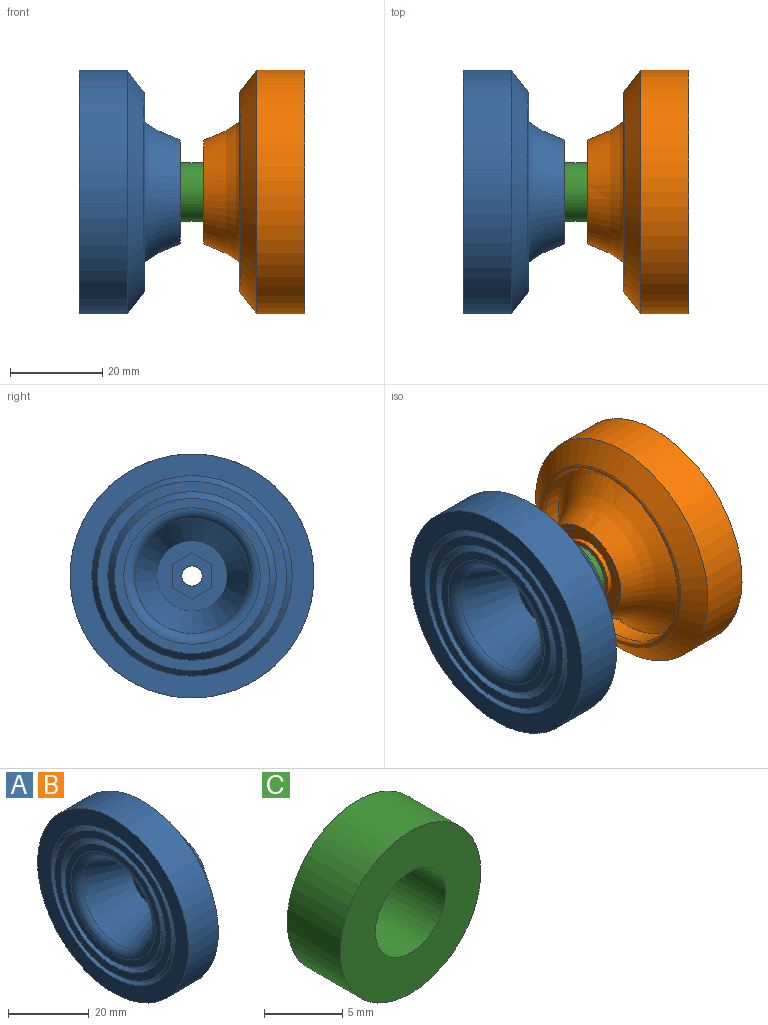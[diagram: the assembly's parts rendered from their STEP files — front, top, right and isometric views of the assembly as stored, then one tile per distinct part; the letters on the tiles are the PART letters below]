
ASSEMBLY  parts=3 mates=2
PART A: 34 faces, bbox 28.5x72.3x72.3 mm
  f0: cylinder r=2.2mm len=5.87mm, axis (1,0,0), area 81.1mm2, adj f17,f33
  f1: plane 22.55x22.55mm, normal (1,0,0), area 66.1mm2, adj f2,f26
  f2: torus R=33.4mm, axis (1,0,0), area 1516.3mm2, adj f1,f3
  f3: cylinder r=20.5mm len=41mm, axis (1,0,0), area 519.1mm2, adj f2,f4
  f4: torus R=21.3mm, axis (1,0,0), area 237.4mm2, adj f3,f5
  f5: torus R=104.59mm, axis (1,0,0), area 897.4mm2, adj f4,f6
  f6: cylinder r=26.5mm len=53mm, axis (1,0,0), area 1743.5mm2, adj f5,f7
  f7: plane 53x53mm, normal (-1,0,0), area 715.6mm2, adj f6,f8
  f8: cylinder r=21.78mm len=43.56mm, axis (1,0,0), area 273.7mm2, adj f7,f9
  f9: cone r=21.78mm half-angle=31.4deg, axis (1,0,0), area 311.7mm2, adj f8,f10
  f10: plane 41.12x41.12mm, normal (-1,0,0), area 276.3mm2, adj f9,f11
  f11: cylinder r=18.3mm len=36.6mm, axis (1,0,0), area 229.9mm2, adj f10,f12
  f12: cone r=18.3mm half-angle=35.9deg, axis (1,0,0), area 272.7mm2, adj f11,f13
  f13: plane 33.7x33.7mm, normal (-1,0,0), area 202.4mm2, adj f12,f14
  f14: torus R=14.81mm, axis (1,0,0), area 254.7mm2, adj f13,f15
  f15: cone r=12.48mm half-angle=21.1deg, axis (-1,0,0), area 849.5mm2, adj f14,f16
  f16: plane 15.28x15.28mm, normal (-1,0,0), area 118.5mm2, adj f15,f27,f28,f29,f30,f31,f32
  f17: plane 6x6mm, normal (1,0,0), area 13.1mm2, adj f0,f18
  f18: cylinder r=3mm len=6mm, axis (1,0,0), area 33mm2, adj f17,f19
  f19: plane 7.6x7.6mm, normal (1,0,0), area 17.1mm2, adj f18,f20
  f20: cylinder r=3.8mm len=7.6mm, axis (1,0,0), area 17.9mm2, adj f19,f21
  f21: plane 13x13mm, normal (1,0,0), area 87.4mm2, adj f20,f22
  f22: cylinder r=6.5mm len=13mm, axis (1,0,0), area 61.3mm2, adj f21,f23
  f23: plane 14.6x14.6mm, normal (1,0,0), area 34.7mm2, adj f22,f24
  f24: cylinder r=7.3mm len=14.6mm, axis (1,0,0), area 49.3mm2, adj f23,f25
  f25: plane 20.6x20.6mm, normal (1,0,0), area 165.9mm2, adj f24,f26
  f26: cylinder r=10.3mm len=20.6mm, axis (1,0,0), area 69.6mm2, adj f1,f25
  f27: plane 5x3mm, normal (0,1,0), area 15mm2, adj f16,f28,f32,f33
  f28: plane 4.33x3mm, normal (0,0.5,-0.87), area 15mm2, adj f16,f27,f29,f33
  f29: plane 4.33x3mm, normal (0,-0.5,-0.87), area 15mm2, adj f16,f28,f30,f33
  f30: plane 5x3mm, normal (0,-1,0), area 15mm2, adj f16,f29,f31,f33
  f31: plane 4.33x3mm, normal (0,-0.5,0.87), area 15mm2, adj f16,f30,f32,f33
  f32: plane 4.33x3mm, normal (0,0.5,0.87), area 15mm2, adj f16,f27,f31,f33
  f33: plane 10x8.66mm, normal (-1,0,0), area 49.7mm2, adj f0,f27,f28,f29,f30,f31,f32
PART B: same geometry as A
PART C: 4 faces, bbox 12.7x4.8x12.7 mm
  f0: cylinder r=3.17mm len=6.35mm, axis (0,1,0), area 95.7mm2, adj f2,f3
  f1: cylinder r=6.35mm len=12.7mm, axis (0,1,0), area 191.3mm2, adj f2,f3
  f2: plane 12.7x12.7mm, normal (0,-1,0), area 95mm2, adj f0,f1
  f3: plane 12.7x12.7mm, normal (0,1,0), area 95mm2, adj f0,f1
PLACE A t=(-31.33,-13.91,6.22)mm
PLACE B rot(axis=(0,1,0),180deg) t=(-28.28,-13.91,6.22)mm
PLACE C rot(axis=(0.58,0.58,-0.58),120deg) t=(-27.41,-13.91,6.22)mm
MATE fastened B.f0 <-> C.f0  axis (-1,0,0) through (-27.41,-13.91,6.22)mm
MATE fastened C.f0 <-> A.f0  axis (1,0,0) through (-32.2,-13.91,6.22)mm
